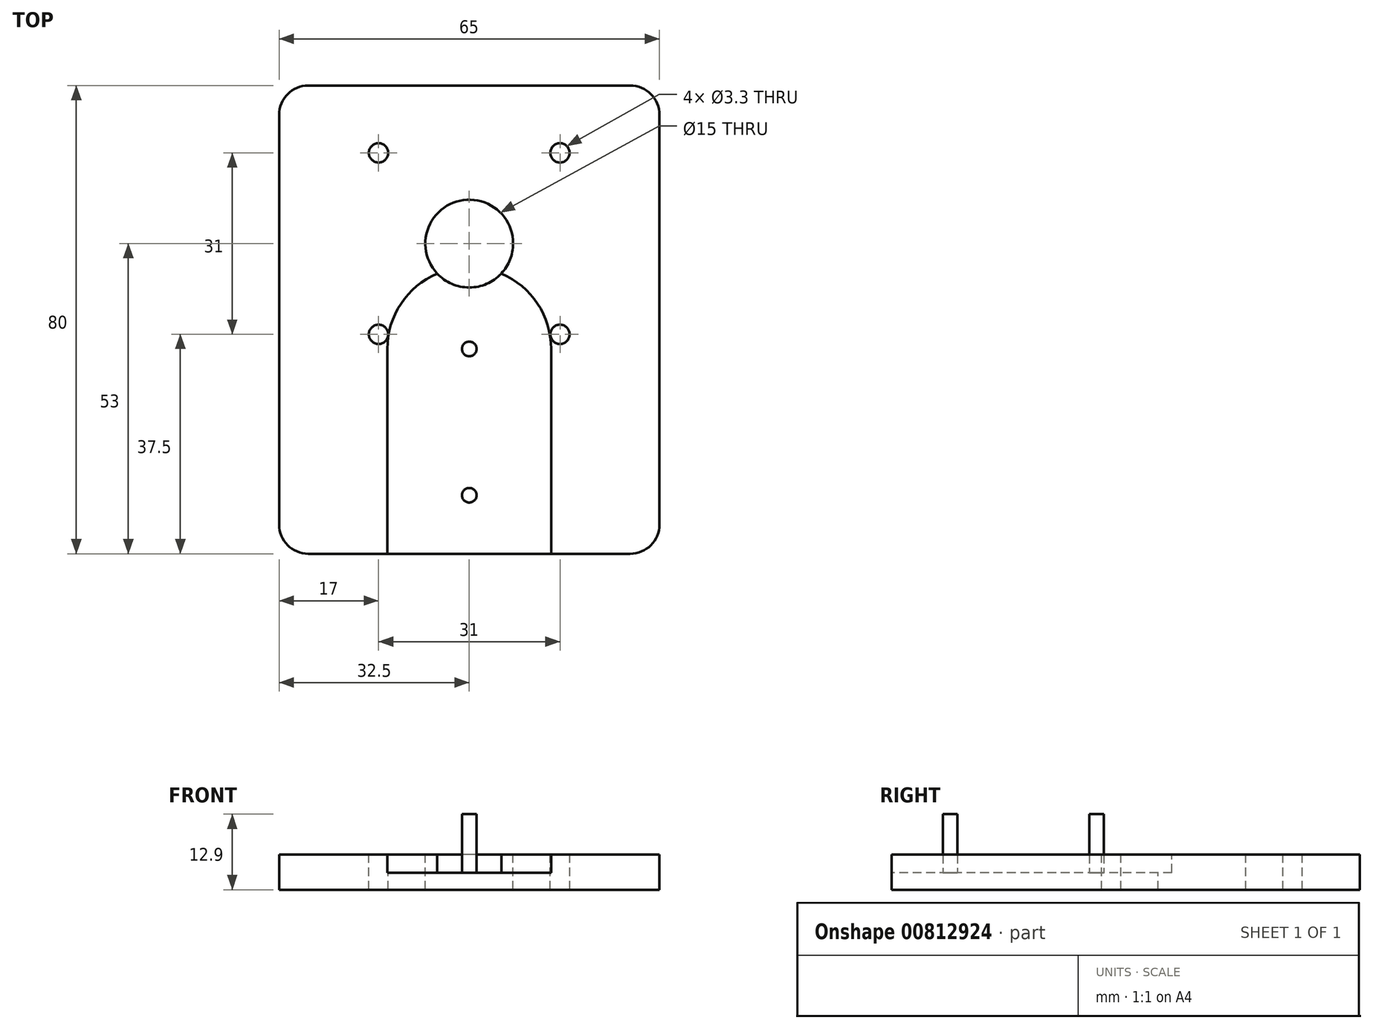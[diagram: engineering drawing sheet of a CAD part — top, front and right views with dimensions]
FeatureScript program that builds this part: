
annotation { "Feature Type Name" : "Feature", "Feature Type Description" : "" }
export const myFeature = defineFeature(function(context is Context, id is Id, definition is map)
    precondition{}
    {
        {
            var Q0;
            Q0=qCreatedBy(makeId("Top.planeOp"),FACE);
            var sketch = newSketch(context, id + "F0", { "sketchPlane" : qUnion([Q0])});
            skLineSegment(sketch, "E0.bottom", {"start": v(32.5, -40) * mm, "end": v(-32.5, -40) * mm});
            skLineSegment(sketch, "E0.top", {"start": v(32.5, 40) * mm, "end": v(-32.5, 40) * mm});
            skLineSegment(sketch, "E0.left", {"start": v(32.5, -40) * mm, "end": v(32.5, 40) * mm});
            skLineSegment(sketch, "E0.right", {"start": v(-32.5, -40) * mm, "end": v(-32.5, 40) * mm});
            skPoint(sketch, "E0.middle", {"position": v(0, 0) * mm});
            skLineSegment(sketch, "E1", {"start": v(0, 40) * mm, "end": v(0, -40) * mm, "construction": true});
            skSolve(sketch);
        }
        {
            var Q0;
            Q0=makeQuery(id+"F0.imprint","IMPRINT",FACE,{"disambiguationData":[TD([[makeQuery(id+"F0.imprint","IMPRINT",EDGE,{"derivedFrom":sQuery(id+"F0.wireOp",EDGE,"E0.bottom")}),-1.0]])]});
            extrude(context, id + "F1", {"entities" : qUnion([Q0]), "depth" : 6 * mm, "offsetDistance" : 25 * mm});
        }
        {
            var Q0;
            Q0=makeQuery(id+"F1.opExtrude","SWEPT_EDGE",EDGE,{"disambiguationData":[OSD([sQuery(id+"F0.wireOp",EDGE,"E0.bottom"),sQuery(id+"F0.wireOp",EDGE,"E0.left")])]});
            var Q1;
            Q1=makeQuery(id+"F1.opExtrude","SWEPT_EDGE",EDGE,{"disambiguationData":[OSD([sQuery(id+"F0.wireOp",EDGE,"E0.top"),sQuery(id+"F0.wireOp",EDGE,"E0.left")])]});
            var Q2;
            Q2=makeQuery(id+"F1.opExtrude","SWEPT_EDGE",EDGE,{"disambiguationData":[OSD([sQuery(id+"F0.wireOp",EDGE,"E0.top"),sQuery(id+"F0.wireOp",EDGE,"E0.right")])]});
            var Q3;
            Q3=makeQuery(id+"F1.opExtrude","SWEPT_EDGE",EDGE,{"disambiguationData":[OSD([sQuery(id+"F0.wireOp",EDGE,"E0.bottom"),sQuery(id+"F0.wireOp",EDGE,"E0.right")])]});
            fillet(context, id + "F2", {"entities" : qUnion([Q0, Q1, Q2, Q3]), "radius" : 5 * mm, "tangentPropagation" : true, "allowEdgeOverflow" : false});
        }
        {
            var Q0;
            Q0=makeQuery(id+"F1.opExtrude","CAP_FACE",FACE,{"disambiguationData":[OSD([sQuery(id+"F0.wireOp",EDGE,"E0.bottom"),sQuery(id+"F0.wireOp",EDGE,"E0.top"),sQuery(id+"F0.wireOp",EDGE,"E0.left"),sQuery(id+"F0.wireOp",EDGE,"E0.right")])],"isStart":false});
            var sketch = newSketch(context, id + "F3", { "sketchPlane" : qUnion([Q0])});
            skArc(sketch, "E2", {"start": v(14, -5) * mm, "mid": v(0, 9) * mm, "end": v(-14, -5) * mm});
            skLineSegment(sketch, "E3", {"start": v(-14, -5) * mm, "end": v(-14, -40) * mm});
            skLineSegment(sketch, "E4", {"start": v(14, -5) * mm, "end": v(14, -40) * mm});
            skLineSegment(sketch, "E5", {"start": v(-14, -40) * mm, "end": v(14, -40) * mm});
            skSolve(sketch);
        }
        {
            var Q0;
            Q0 = qSketchRegion(id + "F3", true);
            extrude(context, id + "F4", {"entities" : qUnion([Q0]), "operationType" : NewBodyOperationType.REMOVE, "oppositeDirection" : true, "depth" : 3.1 * mm, "offsetDistance" : 25 * mm});
        }
        {
            var Q0;
            Q0=makeQuery(id+"F4.boolean.opBoolean","COPY",FACE,{"derivedFrom":makeQuery(id+"F4.opExtrude","CAP_FACE",FACE,{"disambiguationData":[OSD([sQuery(id+"F3.wireOp",EDGE,"E2"),sQuery(id+"F3.wireOp",EDGE,"E3"),sQuery(id+"F3.wireOp",EDGE,"E4"),sQuery(id+"F3.wireOp",EDGE,"E5")])],"isStart":false})});
            var sketch = newSketch(context, id + "F5", { "sketchPlane" : qUnion([Q0])});
            skLineSegment(sketch, "E6", {"start": v(0, -40) * mm, "end": v(0, 9) * mm, "construction": true});
            skCircle(sketch, "E7", {"center": v(0, -5) * mm, "radius": 1.25 * mm});
            skCircle(sketch, "E8", {"center": v(0, -30) * mm, "radius": 1.25 * mm});
            skSolve(sketch);
        }
        {
            var Q0;
            Q0 = qSketchRegion(id + "F5", true);
            extrude(context, id + "F6", {"entities" : qUnion([Q0]), "operationType" : NewBodyOperationType.ADD, "depth" : 10 * mm, "offsetDistance" : 25 * mm});
        }
        {
            var Q0;
            Q0=makeQuery(id+"F1.opExtrude","CAP_FACE",FACE,{"disambiguationData":[OSD([sQuery(id+"F0.wireOp",EDGE,"E0.bottom"),sQuery(id+"F0.wireOp",EDGE,"E0.top"),sQuery(id+"F0.wireOp",EDGE,"E0.left"),sQuery(id+"F0.wireOp",EDGE,"E0.right")])],"isStart":true});
            var sketch = newSketch(context, id + "F7", { "sketchPlane" : qUnion([Q0])});
            skLineSegment(sketch, "E9", {"start": v(0, 40) * mm, "end": v(0, -40) * mm, "construction": true});
            skPoint(sketch, "E10", {"position": v(-15.5, 2.5) * mm});
            skPoint(sketch, "E11", {"position": v(15.5, 2.5) * mm});
            skPoint(sketch, "E12", {"position": v(-15.5, -28.5) * mm});
            skPoint(sketch, "E13", {"position": v(15.5, -28.5) * mm});
            skCircle(sketch, "E14", {"center": v(0, -13) * mm, "radius": 7.25 * mm, "construction": true});
            skCircle(sketch, "E15.0", {"center": v(0, 5) * mm, "radius": 1.25 * mm, "construction": true});
            skSolve(sketch);
        }
        {
            var Q0;
            Q0=sQuery(id+"F7.wireOp",VERTEX,"E14.center");
            var Q1;
            Q1=makeQuery(id+"F1.opExtrude","SWEPT_BODY",BODY,{"disambiguationData":[OSD([sQuery(id+"F0.wireOp",EDGE,"E0.bottom"),sQuery(id+"F0.wireOp",EDGE,"E0.top"),sQuery(id+"F0.wireOp",EDGE,"E0.left"),sQuery(id+"F0.wireOp",EDGE,"E0.right")])]});
            hole(context, id + "F8", {"style" : HoleStyle.SIMPLE, "endStyle" : HoleEndStyle.THROUGH, "holeDiameter" : 15 * mm, "majorDiameter" : 5 * mm, "isTappedThrough" : true, "tappedDepth" : 12 * mm, "tapClearance" : 3, "locations" : qUnion([Q0]), "scope" : qUnion([Q1])});
        }
        {
            var Q0;
            Q0=sQuery(id+"F7.wireOp",VERTEX,"E13");
            var Q1;
            Q1=sQuery(id+"F7.wireOp",VERTEX,"E11");
            var Q2;
            Q2=sQuery(id+"F7.wireOp",VERTEX,"E10");
            var Q3;
            Q3=sQuery(id+"F7.wireOp",VERTEX,"E12");
            var Q4;
            Q4=makeQuery(id+"F1.opExtrude","SWEPT_BODY",BODY,{"disambiguationData":[OSD([sQuery(id+"F0.wireOp",EDGE,"E0.bottom"),sQuery(id+"F0.wireOp",EDGE,"E0.top"),sQuery(id+"F0.wireOp",EDGE,"E0.left"),sQuery(id+"F0.wireOp",EDGE,"E0.right")])]});
            hole(context, id + "F9", {"style" : HoleStyle.SIMPLE, "endStyle" : HoleEndStyle.THROUGH, "standardTappedOrClearance" : lookupTablePath({ "standard" : "ISO", "fit" : "Normal", "size" : "M3", "type" : "Clearance" }), "standardBlindInLast" : lookupTablePath({ "fit" : "Standard", "standard" : "ISO", "size" : "M3", "type" : "Clearance" }), "holeDiameter" : 3.3 * mm, "majorDiameter" : 5 * mm, "isTappedThrough" : true, "tappedDepth" : 12 * mm, "tapClearance" : 3, "locations" : qUnion([Q0, Q1, Q2, Q3]), "scope" : qUnion([Q4])});
        }
    });
